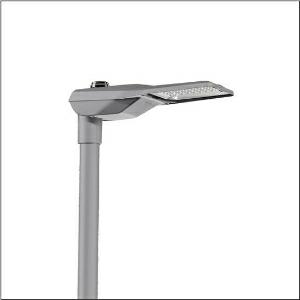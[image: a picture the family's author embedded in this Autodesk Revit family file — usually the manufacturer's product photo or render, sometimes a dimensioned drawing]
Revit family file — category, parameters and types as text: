
# Revit family: streetlight_sl_21_mini___st0_5a_5xe6b47n08jb_72a7
name_source: partatom
category: Lighting Fixtures
units: mm (PartAtom-declared; Revit-internal decimal feet)

## family parameters
Cut with Voids When Loaded = No
Host = Face
Light Source = No
Part Type = Normal
Room Calculation Point = No
Round Connector Dimension = Use Diameter
Shared = No

## types (1)
- --- (1 x LED, 13390 lm, 87.3 W, 4000K)
    Apparent Load = 87 VA
    CIE Flux Codes = 43 76 97 100 100
    Color Rendering = 70
    Color Temperature = 4000K
    Default Elevation = 1800 mm
    Description = Streetlight SL 21 mini, mast luminaire, primary light control with lens, of PMMA, primary optical cover: cover, of toughened safety glass, transparent, light distribution: ST0.5a, light emission: direct distribution, primary light characteristic: asymmetric, installation type: side-entry, LED, 3G 2.5mm², High Power LED, rated luminous flux: 13.390lm, luminous efficacy: 153lm/W, light colour: 740, colour temperature: 4000K, control gear: NEMA (7pin), control: overheat protection, pre-setting: linear dimming characteristic, constant luminous flux control, time-dependent luminous flux control, flexible luminous flux parameterisation, mains connection: 230..240V, AC, 50/60Hz, connection cable pre-assembled, cable length: 10,5m, wiring characteristics: H05VV-F, start of lifetime: 87W, end of service life: 90W, reduction: 40W, luminaire housing, of diecast aluminium (EN AC-44300), powder-coated, SITECO metallic grey (DB 702S), corrosivity category C5 high according to DIN EN ISO 12944, multi-level sealing system, sealing non-destructively replaceable, inclination adjustable: 0°, 5°, 10°, 15°, length: 628mm, width: 235mm, height: 110mm, spigot size: 42mm (side-entry), mounting height: 4..8m, protection rating (complete): IP66, insulation class (complete): insulation class I (protective earthing), certification: CE, ENEC, ENEC+, VDE, impact resistance: IK10, permissible operating ambient temperature for outdoor applications: -40..+50°C, standard-compliant lighting for roads and squares, packaging unit: 1 piece

Light Distribution: ST0.5a
    Height = 110 mm
    Lamp = 1 x LED
    Lamp Light Flux = 13390 lm
    Lamp Power = 87.3 W
    Lamp count = 1
    Length = 625 mm
    Luminous efficacy = 153 lm/W
    Manufacturer = Siteco
    ModVariant = No
    Model = 5XE6B47N08JB
    Number of Poles = 1
    OnlyDefault = Yes
    Power Factor = 1
    Product Name = Streetlight SL 21 mini | ST0.5a
    Product group = mast luminaire | pylon top
    ProductGroupID = 6100
    Protection Class = Protection class I
    Protection Degree = IP 66
    RLX_Detail_Level = 1
    RLX_Emergency_Light_Flux = 0 lm
    RLX_Emergency_Type = 0
    RLX_Emergency_Type_DB = No
    RlxData = <blob elided: 37253 chars, md5=ba1d9bb9>
    Socket = socket
    Standby Power = 0 W
    System Light Flux = 13390 lm
    System Power = 87 W
    Type Comments = factory setting: luminous flux: 100 % | dim-lin: 254 | 915 mA
    Type Image = l_1294379.jpg
    URL = http://relux.com
    VarID = @adj_136225
    Voltage = 0 V
    Weight = 0.00 kg
    Width = 234 mm

## geometry (parser evidence)
native form markers: Blend x4, Sweep x11
no freeform markers — native parametric forms only
